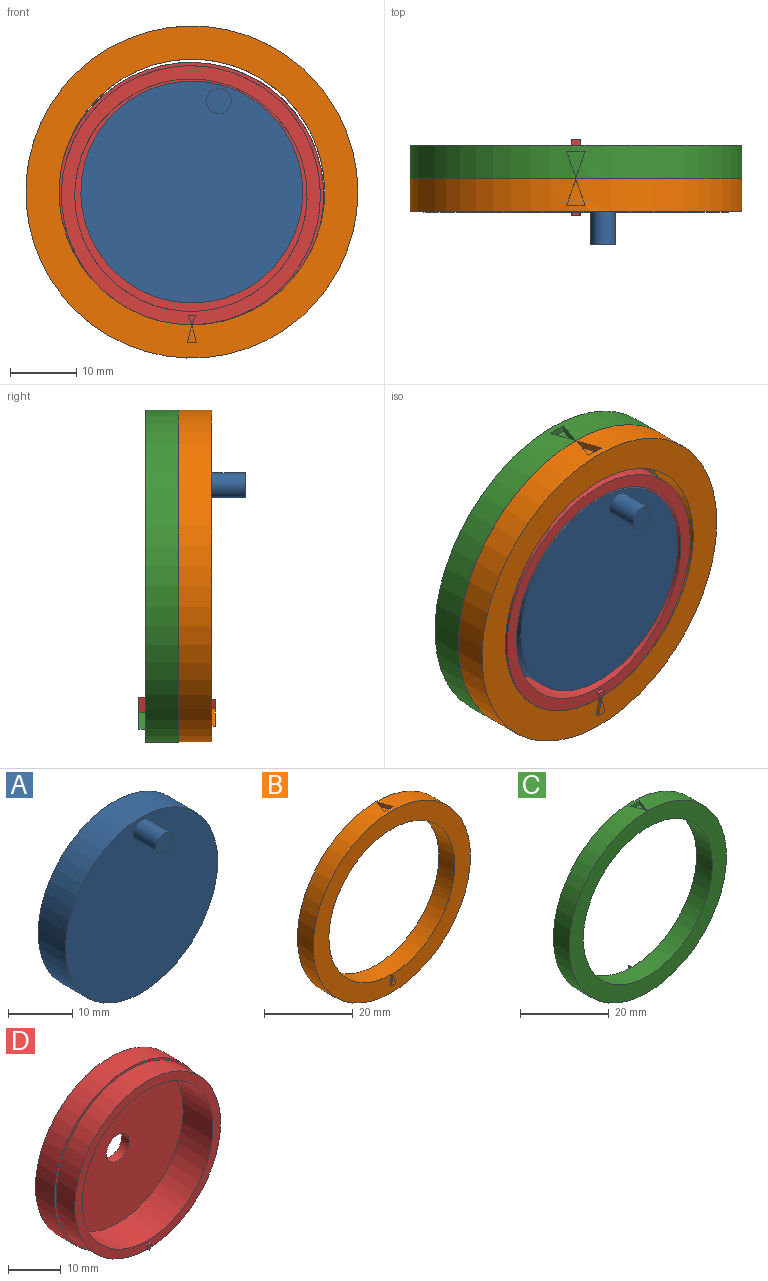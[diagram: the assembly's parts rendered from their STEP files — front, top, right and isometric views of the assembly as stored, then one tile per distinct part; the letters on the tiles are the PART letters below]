
ASSEMBLY  parts=4 mates=3
PART A: 7 faces, bbox 33.4x15x33.4 mm
  f0: cylinder r=2.68mm len=5.35mm, axis (0,-1,0), area 67.3mm2, adj f1,f3
  f1: plane 5.35x5.35mm, normal (0,1,0), area 22.5mm2, adj f0
  f2: cylinder r=16.71mm len=33.42mm, axis (0,-1,0), area 630mm2, adj f3,f4
  f3: plane 33.42x33.42mm, normal (0,1,0), area 854.8mm2, adj f0,f2
  f4: plane 33.42x33.42mm, normal (0,-1,0), area 866.4mm2, adj f2,f5
  f5: cylinder r=1.87mm len=5mm, axis (0,1,0), area 58.6mm2, adj f4,f6
  f6: plane 3.73x3.73mm, normal (0,-1,0), area 10.9mm2, adj f5
PART B: 12 faces, bbox 50x5.5x50 mm
  f0: plane 50x50mm, normal (0,-1,0), area 705mm2, adj f1,f2,f8,f9,f10
  f1: cylinder r=25mm len=50mm, axis (0,-1,0), area 779.8mm2, adj f0,f3,f4,f5,f6
  f2: cylinder r=20mm len=40mm, axis (0,-1,0), area 628.3mm2, adj f0,f3
  f3: plane 50x50mm, normal (0,1,0), area 706.9mm2, adj f1,f2
  f4: plane 3.97x1.41mm, normal (-0.94,-0.33,0), area 4.2mm2, adj f1,f5,f6,f7
  f5: plane 3.97x1.41mm, normal (0.94,-0.33,0), area 4.2mm2, adj f1,f4,f6,f7
  f6: plane 2.82x1mm, normal (0,1,0), area 2.8mm2, adj f1,f4,f5,f7
  f7: plane 3.96x2.82mm, normal (0,0,1), area 5.6mm2, adj f4,f5,f6
  f8: plane 1.39x0.5mm, normal (0,0,-1), area 0.7mm2, adj f0,f9,f10,f11
  f9: plane 2.65x0.7mm, normal (0.97,0,0.25), area 1.4mm2, adj f0,f8,f10,f11
  f10: plane 2.65x0.7mm, normal (-0.97,0,0.25), area 1.4mm2, adj f0,f8,f9,f11
  f11: plane 2.65x1.39mm, normal (0,-1,0), area 1.8mm2, adj f8,f9,f10
PART C: 12 faces, bbox 50x6x50 mm
  f0: plane 50x50mm, normal (0,1,0), area 641.4mm2, adj f1,f2,f4,f5,f6
  f1: cylinder r=20.5mm len=41mm, axis (0,-1,0), area 644mm2, adj f0,f3
  f2: cylinder r=25mm len=50mm, axis (0,-1,0), area 779.7mm2, adj f0,f3,f8,f9,f10
  f3: plane 50x50mm, normal (0,-1,0), area 643.2mm2, adj f1,f2
  f4: plane 2.59x1mm, normal (-0.96,0,0.26), area 2.7mm2, adj f0,f5,f6,f7
  f5: plane 2.59x1mm, normal (0.96,0,0.26), area 2.7mm2, adj f0,f4,f6,f7
  f6: plane 1.42x1mm, normal (0,0,-1), area 1.4mm2, adj f0,f4,f5,f7
  f7: plane 2.59x1.42mm, normal (0,1,0), area 1.8mm2, adj f4,f5,f6
  f8: plane 4.02x1.41mm, normal (0.94,0.33,0), area 4.2mm2, adj f2,f9,f10,f11
  f9: plane 4.02x1.41mm, normal (-0.94,0.33,0), area 4.2mm2, adj f2,f8,f10,f11
  f10: plane 2.82x1mm, normal (0,-1,0), area 2.8mm2, adj f2,f8,f9,f11
  f11: plane 4.01x2.82mm, normal (0,0,1), area 5.7mm2, adj f8,f9,f10
PART D: 16 faces, bbox 40x11.5x40 mm
  f0: plane 39x39mm, normal (0,-1,0), area 231.7mm2, adj f2,f5,f12,f13,f14
  f1: plane 40x40mm, normal (0,1,0), area 1226.1mm2, adj f3,f7,f8,f9,f10
  f2: cylinder r=17.5mm len=35mm, axis (0,1,0), area 879.6mm2, adj f0,f6
  f3: cylinder r=20mm len=40mm, axis (0,1,0), area 628.3mm2, adj f1,f4
  f4: plane 40x40mm, normal (0,-1,0), area 62mm2, adj f3,f5
  f5: cylinder r=19.5mm len=39mm, axis (0,1,0), area 612.6mm2, adj f0,f4
  f6: plane 35x35mm, normal (0,-1,0), area 933.1mm2, adj f2,f7
  f7: cylinder r=3.04mm len=6.08mm, axis (0,1,0), area 38.2mm2, adj f1,f6
  f8: plane 2.25x1mm, normal (-0.96,0,-0.29), area 2.4mm2, adj f1,f9,f10,f11
  f9: plane 1.39x1mm, normal (0,0,1), area 1.4mm2, adj f1,f8,f10,f11
  f10: plane 2.25x1mm, normal (0.96,0,-0.29), area 2.4mm2, adj f1,f8,f9,f11
  f11: plane 2.25x1.39mm, normal (0,1,0), area 1.6mm2, adj f8,f9,f10
  f12: plane 1.39x0.56mm, normal (-0.93,0,-0.37), area 0.8mm2, adj f0,f13,f14,f15
  f13: plane 1.39x0.56mm, normal (0.93,0,-0.37), area 0.8mm2, adj f0,f12,f14,f15
  f14: plane 1.12x0.5mm, normal (0,0,1), area 0.6mm2, adj f0,f12,f13,f15
  f15: plane 1.39x1.12mm, normal (0,-1,0), area 0.8mm2, adj f12,f13,f14
PLACE A rot(axis=(0,1,0),16.6deg) t=(0,0,0)mm
PLACE B at identity fixed
PLACE C rot(axis=(0,-1,0),0deg) t=(0,0,0)mm
PLACE D rot(axis=(0,-1,0),0.4deg) t=(-0.15,0,0.02)mm
MATE revolute D.f2 <-> A.f0  axis (0,1,0) through (-0.14,10,-0.48)mm
MATE revolute A.f2 <-> B.f1  axis (0,-1,0) through (0,0,0)mm
MATE revolute C.f1 <-> B.f1  axis (0,-1,0) through (0,5,0)mm
